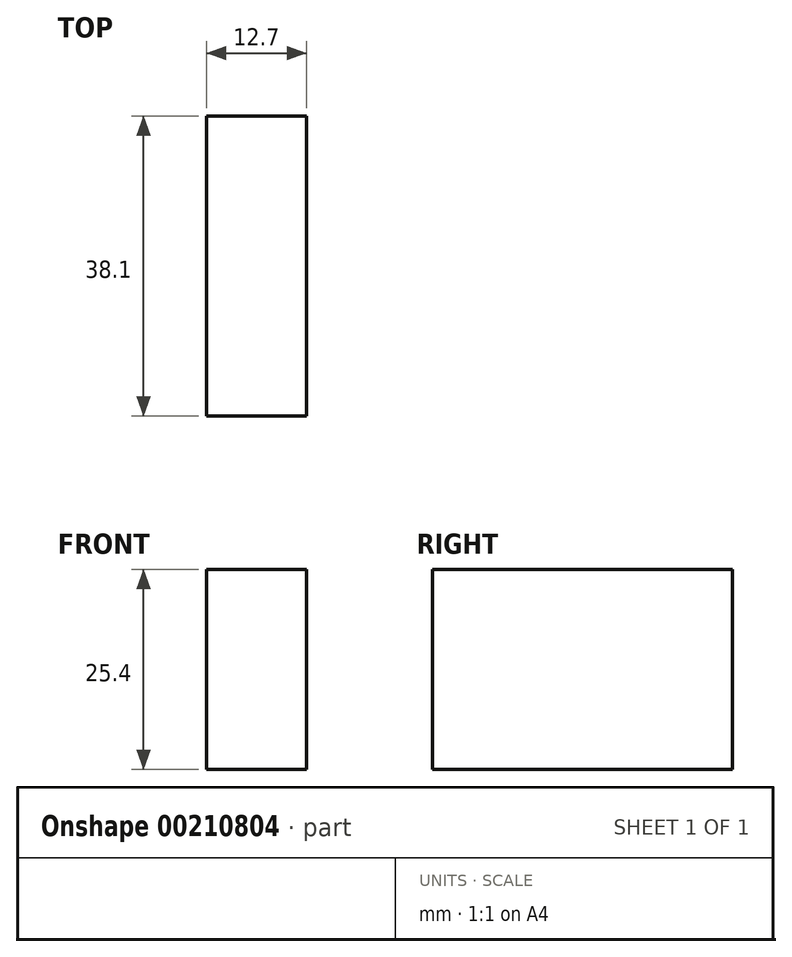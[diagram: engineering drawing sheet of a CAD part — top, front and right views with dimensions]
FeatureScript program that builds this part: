
annotation { "Feature Type Name" : "Feature", "Feature Type Description" : "" }
export const myFeature = defineFeature(function(context is Context, id is Id, definition is map)
    precondition{}
    {
        {
            var Q0;
            Q0=qCreatedBy(makeId("Top.planeOp"),FACE);
            var sketch = newSketch(context, id + "F0", { "sketchPlane" : qUnion([Q0])});
            skLineSegment(sketch, "E0.bottom", {"start": v(0, 0) * mm, "end": v(12.7, 0) * mm});
            skLineSegment(sketch, "E0.top", {"start": v(0, 38.1) * mm, "end": v(12.7, 38.1) * mm});
            skLineSegment(sketch, "E0.left", {"start": v(0, 0) * mm, "end": v(0, 38.1) * mm});
            skLineSegment(sketch, "E0.right", {"start": v(12.7, 0) * mm, "end": v(12.7, 38.1) * mm});
            skSolve(sketch);
        }
        {
            var Q0;
            Q0=makeQuery(id+"F0.imprint","IMPRINT",FACE,{"disambiguationData":[TD([[makeQuery(id+"F0.imprint","IMPRINT",EDGE,{"derivedFrom":sQuery(id+"F0.wireOp",EDGE,"E0.bottom")}),1.0]])]});
            extrude(context, id + "F1", {"entities" : qUnion([Q0]), "depth" : 25.4 * mm});
        }
    });
